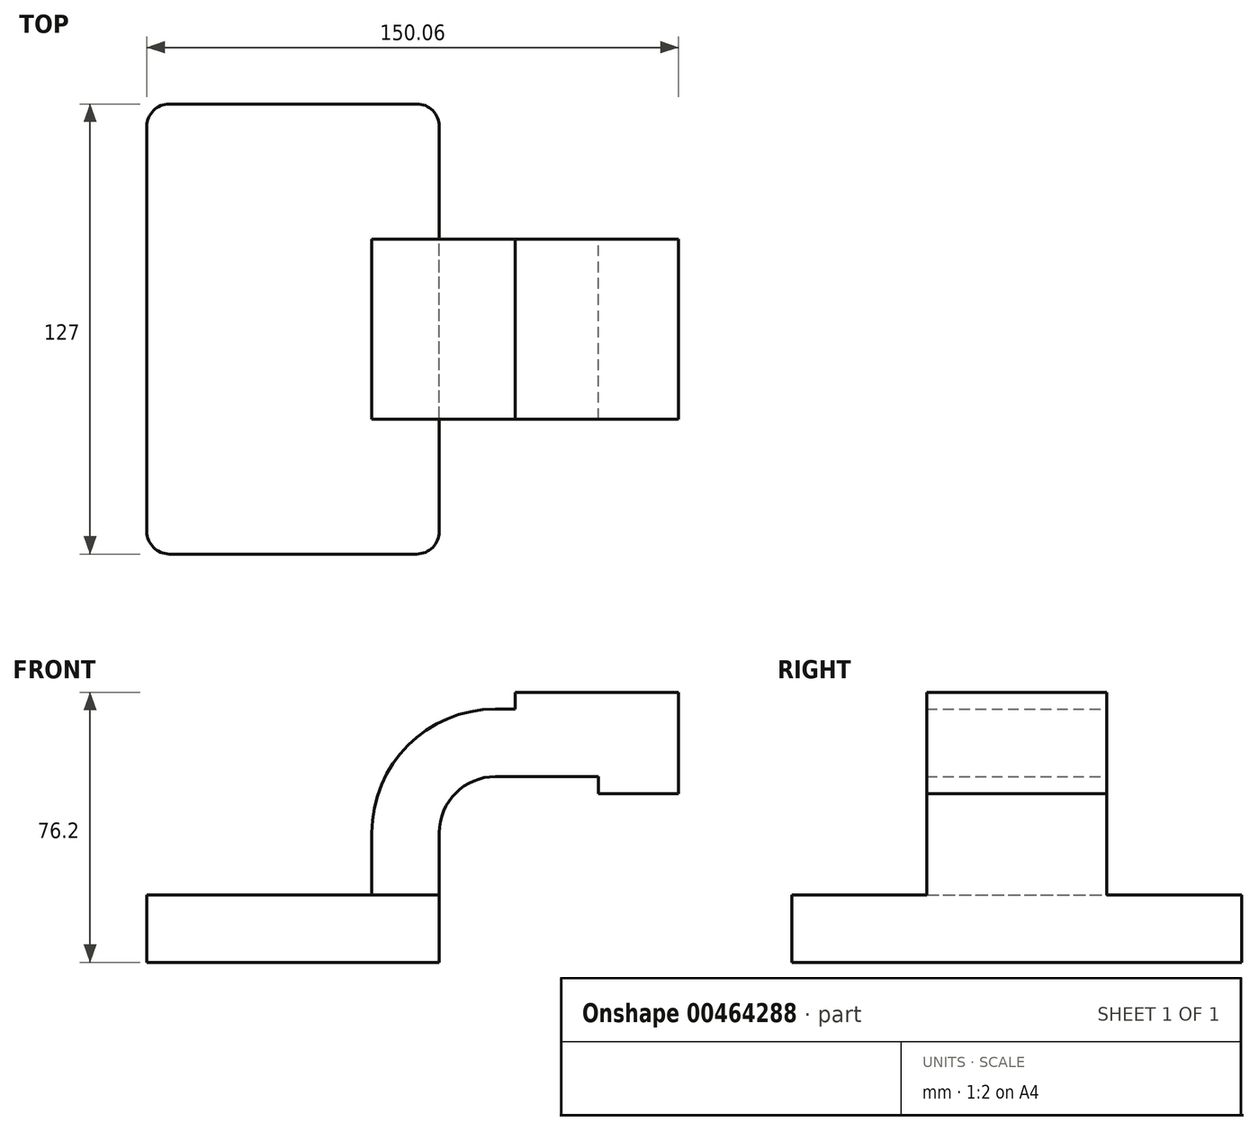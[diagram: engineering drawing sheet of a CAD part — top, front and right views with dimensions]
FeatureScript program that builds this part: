
annotation { "Feature Type Name" : "Feature", "Feature Type Description" : "" }
export const myFeature = defineFeature(function(context is Context, id is Id, definition is map)
    precondition{}
    {
        {
            var Q0;
            Q0=qCreatedBy(makeId("Front.planeOp"),FACE);
            var sketch = newSketch(context, id + "F0", { "sketchPlane" : qUnion([Q0])});
            skLineSegment(sketch, "E0.bottom", {"start": v(41.27, 9.53) * mm, "end": v(-41.28, 9.53) * mm});
            skLineSegment(sketch, "E0.top", {"start": v(41.28, -9.52) * mm, "end": v(-41.27, -9.52) * mm});
            skLineSegment(sketch, "E0.left", {"start": v(41.28, 9.53) * mm, "end": v(41.28, -9.52) * mm});
            skLineSegment(sketch, "E0.right", {"start": v(-41.28, 9.53) * mm, "end": v(-41.27, -9.52) * mm});
            skPoint(sketch, "E0.middle", {"position": v(0, 0) * mm});
            skLineSegment(sketch, "E1.bottom", {"start": v(62.66, 38.1) * mm, "end": v(108.8, 38.1) * mm});
            skLineSegment(sketch, "E1.top", {"start": v(62.66, 66.68) * mm, "end": v(108.8, 66.68) * mm});
            skLineSegment(sketch, "E1.left", {"start": v(62.66, 38.1) * mm, "end": v(62.66, 66.68) * mm});
            skLineSegment(sketch, "E1.right", {"start": v(108.8, 38.1) * mm, "end": v(108.8, 66.68) * mm});
            skPoint(sketch, "E1.middle", {"position": v(85.72, 52.39) * mm});
            skLineSegment(sketch, "E2", {"start": v(41.27, 9.53) * mm, "end": v(41.27, 27) * mm});
            skArc(sketch, "E3", {"start": v(41.27, 27) * mm, "mid": v(45.92, 38.23) * mm, "end": v(57.15, 42.88) * mm});
            skLineSegment(sketch, "E4", {"start": v(57.15, 42.88) * mm, "end": v(86.2, 42.88) * mm});
            skLineSegment(sketch, "E5.0", {"start": v(57.15, 61.93) * mm, "end": v(86.2, 61.93) * mm});
            skArc(sketch, "E5.1", {"start": v(22.23, 27) * mm, "mid": v(32.45, 51.7) * mm, "end": v(57.15, 61.93) * mm});
            skLineSegment(sketch, "E5.2", {"start": v(22.22, 9.53) * mm, "end": v(22.22, 27) * mm});
            skLineSegment(sketch, "E6", {"start": v(86.2, 38.1) * mm, "end": v(86.2, 66.68) * mm});
            skFitSpline(sketch, "E7", {"points": [v(-41.28, 9.53) * mm, v(57.15, 61.93) * mm], "startDerivative": vector(10.15, 68.45) * mm, "endDerivative": vector(171.45, -13.5) * mm});
            skSolve(sketch);
        }
        {
            var Q0;
            Q0=makeQuery(id+"F0.imprint","IMPRINT",FACE,{"disambiguationData":[TD([[makeQuery(id+"F0.imprint","IMPRINT",EDGE,{"derivedFrom":sQuery(id+"F0.wireOp",EDGE,"E0.top")}),-1.0]])]});
            extrude(context, id + "F1", {"entities" : qUnion([Q0]), "endBound" : BoundingType.SYMMETRIC, "depth" : 127 * mm});
        }
        {
            var Q0;
            {var subQ1=sQuery(id+"F0.wireOp",EDGE,"E2");Q0=makeQuery(id+"F0.imprint","IMPRINT",FACE,{"disambiguationData":[TD([[makeQuery(id+"F0.imprint","IMPRINT",EDGE,{"derivedFrom":subQ1}),1.0]])]});}
            var Q1;
            {var subQ0=sQuery(id+"F0.wireOp",EDGE,"E4");var subQ1=sQuery(id+"F0.wireOp",EDGE,"E1.left");var subQ2=makeQuery(id+"F0.imprint","INTERSECT",VERTEX,{"derivedFrom":[subQ1,subQ0]});Q1=makeQuery(id+"F0.imprint","IMPRINT",FACE,{"disambiguationData":[TD([[makeQuery(id+"F0.imprint","IMPRINT",EDGE,{"disambiguationData":[TD([[subQ2,-1.0]])],"derivedFrom":subQ1}),-1.0]])]});}
            var Q2;
            {var subQ0=sQuery(id+"F0.wireOp",EDGE,"E1.right");Q2=makeQuery(id+"F0.imprint","IMPRINT",FACE,{"disambiguationData":[TD([[makeQuery(id+"F0.imprint","IMPRINT",EDGE,{"derivedFrom":subQ0}),1.0]])]});}
            var Q3;
            {var subQ0=sQuery(id+"F0.wireOp",EDGE,"E1.left");var subQ1=sQuery(id+"F0.wireOp",EDGE,"E1.top");var subQ2=makeQuery(id+"F0.imprint","INTERSECT",VERTEX,{"derivedFrom":[subQ1,subQ0]});Q3=makeQuery(id+"F0.imprint","IMPRINT",FACE,{"disambiguationData":[TD([[makeQuery(id+"F0.imprint","IMPRINT",EDGE,{"disambiguationData":[TD([[subQ2,-1.0]])],"derivedFrom":subQ1}),-1.0]])]});}
            extrude(context, id + "F2", {"entities" : qUnion([Q0, Q1, Q2, Q3]), "operationType" : NewBodyOperationType.ADD, "endBound" : BoundingType.SYMMETRIC, "depth" : 50.8 * mm});
        }
        {
            var Q0;
            Q0=makeQuery(id+"F0.imprint","IMPRINT",FACE,{"disambiguationData":[TD([[makeQuery(id+"F0.imprint","IMPRINT",EDGE,{"derivedFrom":sQuery(id+"F0.wireOp",EDGE,"E5.1")}),1.0]])]});
            extrude(context, id + "F3", {"entities" : qUnion([Q0]), "operationType" : NewBodyOperationType.ADD, "endBound" : BoundingType.SYMMETRIC, "depth" : 15.88 * mm});
        }
        {
            var Q0;
            Q0=makeQuery(id+"F1.opExtrude","CAP_EDGE",EDGE,{"disambiguationData":[OSD([sQuery(id+"F0.wireOp",EDGE,"E0.left")])],"isStart":true});
            var Q1;
            Q1=makeQuery(id+"F1.opExtrude","CAP_EDGE",EDGE,{"disambiguationData":[OSD([sQuery(id+"F0.wireOp",EDGE,"E0.right")])],"isStart":true});
            var Q2;
            Q2=makeQuery(id+"F1.opExtrude","CAP_EDGE",EDGE,{"disambiguationData":[OSD([sQuery(id+"F0.wireOp",EDGE,"E0.left")])],"isStart":false});
            var Q3;
            Q3=makeQuery(id+"F1.opExtrude","CAP_EDGE",EDGE,{"disambiguationData":[OSD([sQuery(id+"F0.wireOp",EDGE,"E0.right")])],"isStart":false});
            fillet(context, id + "F4", {"entities" : qUnion([Q0, Q1, Q2, Q3]), "radius" : 6.35 * mm, "tangentPropagation" : true, "allowEdgeOverflow" : false});
        }
    });
